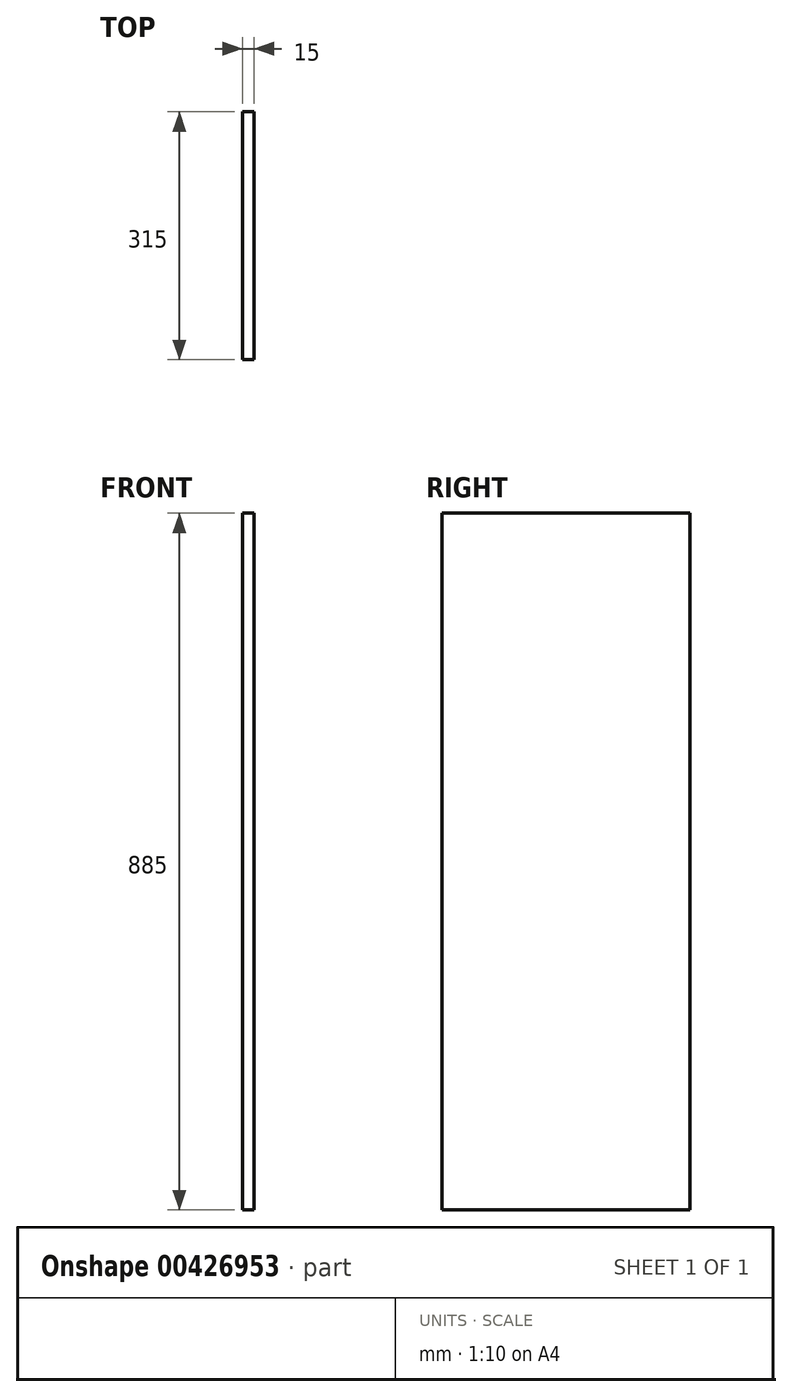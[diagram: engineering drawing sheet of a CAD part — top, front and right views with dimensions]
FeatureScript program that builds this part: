
annotation { "Feature Type Name" : "Feature", "Feature Type Description" : "" }
export const myFeature = defineFeature(function(context is Context, id is Id, definition is map)
    precondition{}
    {
        {
            var Q0;
            Q0=qCreatedBy(makeId("Right.planeOp"),FACE);
            var sketch = newSketch(context, id + "F0", { "sketchPlane" : qUnion([Q0])});
            skLineSegment(sketch, "E0.bottom", {"start": v(-783.1, -188.23) * mm, "end": v(-468.1, -188.23) * mm});
            skLineSegment(sketch, "E0.top", {"start": v(-783.1, -1073.23) * mm, "end": v(-468.1, -1073.23) * mm});
            skLineSegment(sketch, "E0.left", {"start": v(-783.1, -188.23) * mm, "end": v(-783.1, -1073.23) * mm});
            skLineSegment(sketch, "E0.right", {"start": v(-468.1, -188.23) * mm, "end": v(-468.1, -1073.23) * mm});
            skSolve(sketch);
        }
        {
            var Q0;
            Q0=makeQuery(id+"F0.imprint","IMPRINT",FACE,{"disambiguationData":[TD([[makeQuery(id+"F0.imprint","IMPRINT",EDGE,{"derivedFrom":sQuery(id+"F0.wireOp",EDGE,"E0.bottom")}),-1.0]])]});
            extrude(context, id + "F1", {"entities" : qUnion([Q0]), "depth" : 15 * mm});
        }
    });
